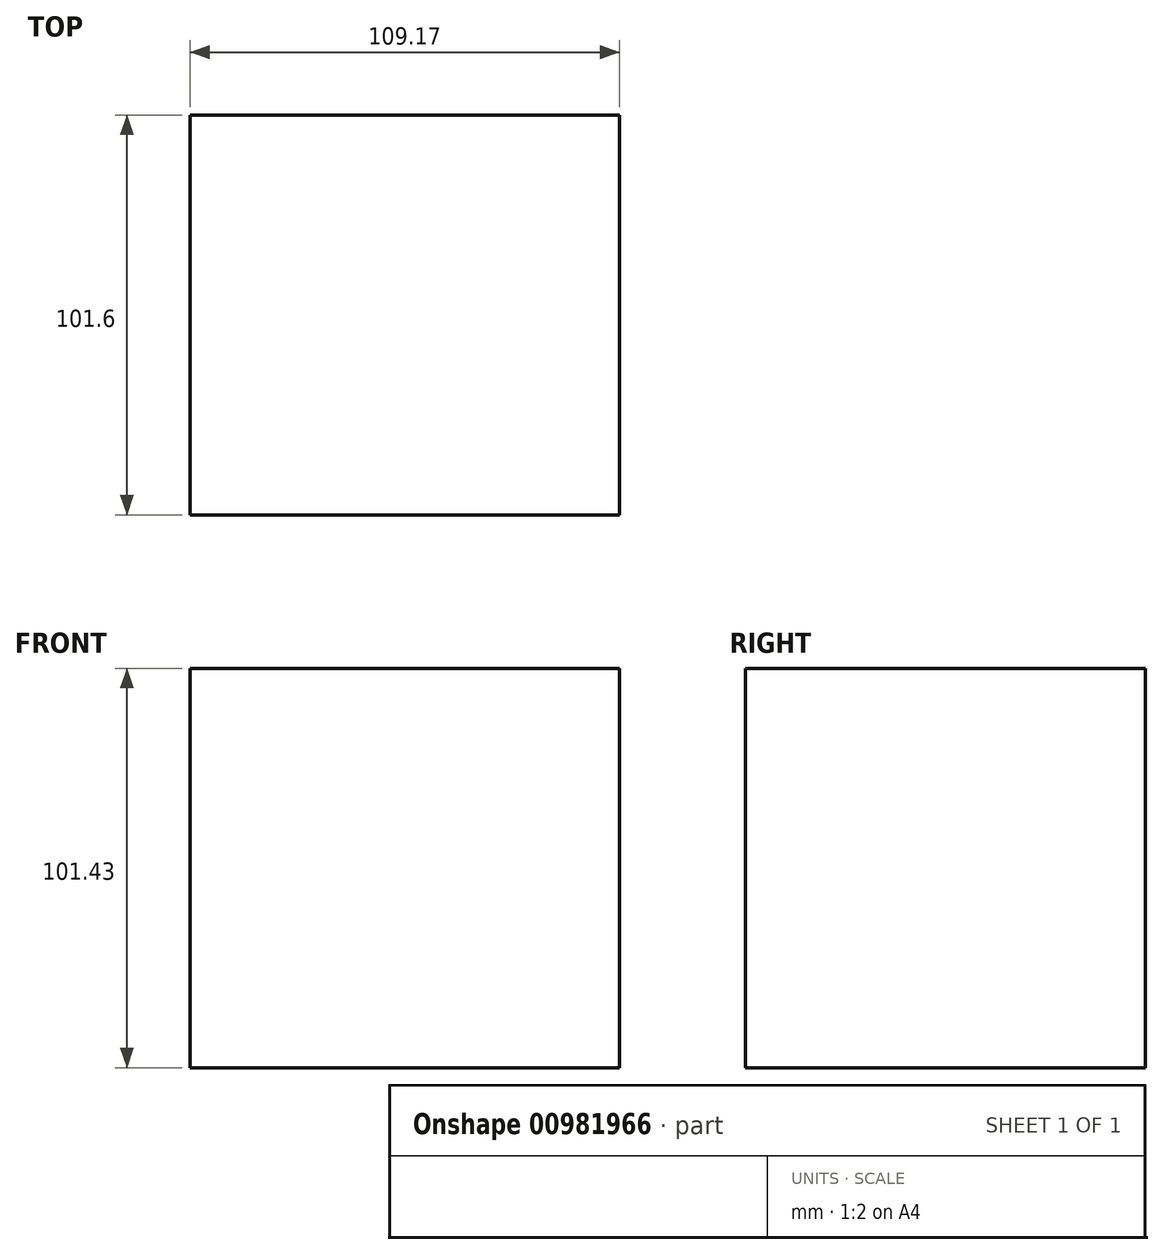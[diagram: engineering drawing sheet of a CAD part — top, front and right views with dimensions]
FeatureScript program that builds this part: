
annotation { "Feature Type Name" : "Feature", "Feature Type Description" : "" }
export const myFeature = defineFeature(function(context is Context, id is Id, definition is map)
    precondition{}
    {
        {
            var Q0;
            Q0=qCreatedBy(makeId("Front.planeOp"),FACE);
            var sketch = newSketch(context, id + "F0", { "sketchPlane" : qUnion([Q0])});
            skLineSegment(sketch, "E0.bottom", {"start": v(-54.29, 48.3) * mm, "end": v(54.88, 48.3) * mm});
            skLineSegment(sketch, "E0.top", {"start": v(-54.29, -53.12) * mm, "end": v(54.88, -53.12) * mm});
            skLineSegment(sketch, "E0.left", {"start": v(-54.29, 48.3) * mm, "end": v(-54.29, -53.12) * mm});
            skLineSegment(sketch, "E0.right", {"start": v(54.88, 48.3) * mm, "end": v(54.88, -53.12) * mm});
            skSolve(sketch);
        }
        {
            var Q0;
            Q0=makeQuery(id+"F0.imprint","IMPRINT",FACE,{"disambiguationData":[TD([[makeQuery(id+"F0.imprint","IMPRINT",EDGE,{"derivedFrom":sQuery(id+"F0.wireOp",EDGE,"E0.bottom")}),-1.0]])]});
            extrude(context, id + "F1", {"entities" : qUnion([Q0]), "depth" : 101.6 * mm, "offsetDistance" : 25.4 * mm});
        }
    });
